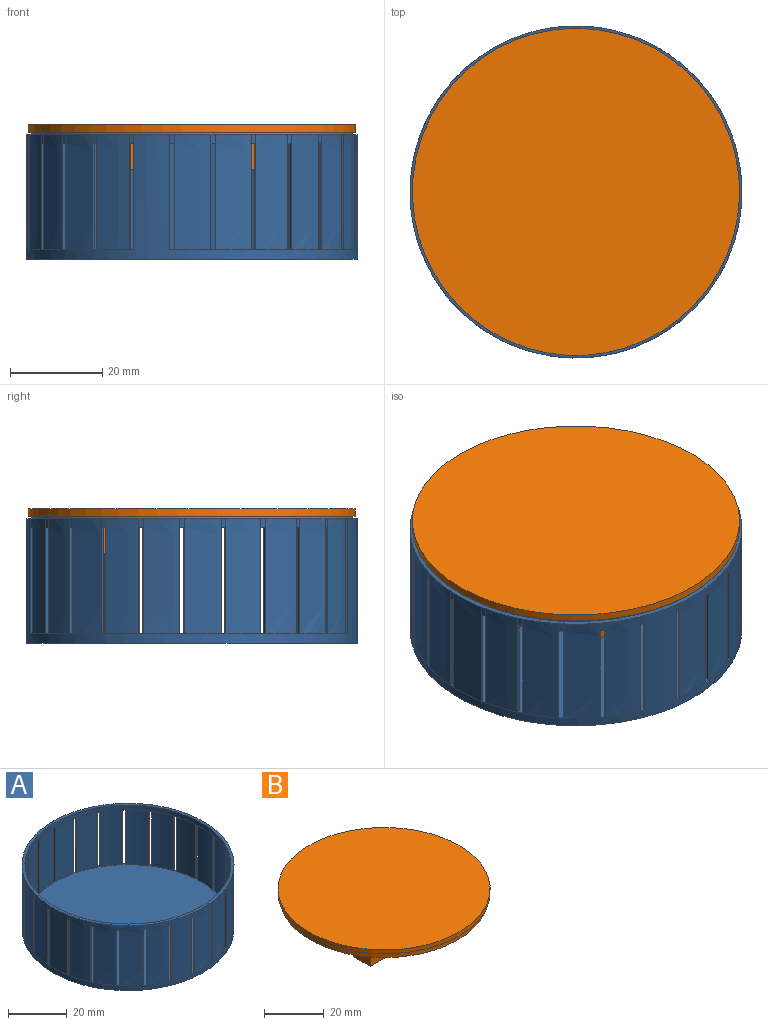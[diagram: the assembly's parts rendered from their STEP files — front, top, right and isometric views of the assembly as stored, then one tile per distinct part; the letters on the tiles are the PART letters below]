
ASSEMBLY  parts=2 mates=1
PART A: 130 faces, bbox 72x72x27 mm
  f0: cylinder r=4mm len=23mm, axis (0,0,-1), area 16.1mm2, adj f74,f75,f102,f129
  f1: cylinder r=4mm len=23mm, axis (0,0,-1), area 16.1mm2, adj f74,f75,f102,f129
  f2: cylinder r=4mm len=23mm, axis (0,0,-1), area 16.1mm2, adj f73,f75,f101,f129
  f3: cylinder r=4mm len=23mm, axis (0,0,-1), area 16.1mm2, adj f73,f75,f101,f129
  f4: cylinder r=4mm len=23mm, axis (0,0,-1), area 16.1mm2, adj f72,f75,f100,f129
  f5: cylinder r=4mm len=23mm, axis (0,0,-1), area 16.1mm2, adj f72,f75,f100,f129
  f6: cylinder r=4mm len=23mm, axis (0,0,-1), area 16.1mm2, adj f71,f75,f99,f129
  f7: cylinder r=4mm len=23mm, axis (0,0,-1), area 16.1mm2, adj f71,f75,f99,f129
  f8: cylinder r=4mm len=23mm, axis (0,0,-1), area 16.1mm2, adj f70,f75,f98,f129
  f9: cylinder r=4mm len=23mm, axis (0,0,-1), area 16.1mm2, adj f70,f75,f98,f129
  f10: cylinder r=4mm len=23mm, axis (0,0,-1), area 16.1mm2, adj f69,f75,f97,f129
  f11: cylinder r=4mm len=23mm, axis (0,0,-1), area 16.1mm2, adj f69,f75,f97,f129
  f12: cylinder r=4mm len=23mm, axis (0,0,-1), area 16.1mm2, adj f68,f75,f96,f129
  f13: cylinder r=4mm len=23mm, axis (0,0,-1), area 16.1mm2, adj f68,f75,f96,f129
  f14: cylinder r=4mm len=23mm, axis (0,0,-1), area 16.1mm2, adj f67,f75,f95,f129
  f15: cylinder r=4mm len=23mm, axis (0,0,-1), area 16.1mm2, adj f67,f75,f95,f129
  f16: cylinder r=4mm len=23mm, axis (0,0,-1), area 16.1mm2, adj f66,f75,f94,f129
  f17: cylinder r=4mm len=23mm, axis (0,0,-1), area 16.1mm2, adj f66,f75,f94,f129
  f18: cylinder r=4mm len=23mm, axis (0,0,-1), area 16.1mm2, adj f64,f75,f93,f129
  f19: cylinder r=4mm len=23mm, axis (0,0,-1), area 16.1mm2, adj f64,f75,f93,f129
  f20: cylinder r=4mm len=23mm, axis (0,0,-1), area 16.1mm2, adj f63,f75,f92,f129
  f21: cylinder r=4mm len=23mm, axis (0,0,-1), area 16.1mm2, adj f63,f75,f92,f129
  f22: cylinder r=4mm len=23mm, axis (0,0,-1), area 16.1mm2, adj f62,f75,f91,f129
  f23: cylinder r=4mm len=23mm, axis (0,0,-1), area 16.1mm2, adj f62,f75,f91,f129
  f24: cylinder r=4mm len=23mm, axis (0,0,-1), area 16.1mm2, adj f61,f75,f90,f129
  f25: cylinder r=4mm len=23mm, axis (0,0,-1), area 16.1mm2, adj f61,f75,f90,f129
  f26: cylinder r=4mm len=23mm, axis (0,0,-1), area 16.1mm2, adj f60,f75,f89,f129
  f27: cylinder r=4mm len=23mm, axis (0,0,-1), area 16.1mm2, adj f60,f75,f89,f129
  f28: cylinder r=4mm len=23mm, axis (0,0,-1), area 16.1mm2, adj f59,f75,f88,f129
  f29: cylinder r=4mm len=23mm, axis (0,0,-1), area 16.1mm2, adj f59,f75,f88,f129
  f30: cylinder r=4mm len=23mm, axis (0,0,-1), area 16.1mm2, adj f58,f75,f87,f129
  f31: cylinder r=4mm len=23mm, axis (0,0,-1), area 16.1mm2, adj f58,f75,f87,f129
  f32: cylinder r=4mm len=23mm, axis (0,0,-1), area 16.1mm2, adj f57,f75,f86,f129
  f33: cylinder r=4mm len=23mm, axis (0,0,-1), area 16.1mm2, adj f57,f75,f86,f129
  f34: cylinder r=4mm len=23mm, axis (0,0,-1), area 16.1mm2, adj f56,f75,f85,f129
  f35: cylinder r=4mm len=23mm, axis (0,0,-1), area 16.1mm2, adj f56,f75,f85,f129
  f36: cylinder r=4mm len=23mm, axis (0,0,-1), area 16.1mm2, adj f55,f75,f84,f129
  f37: cylinder r=4mm len=23mm, axis (0,0,-1), area 16.1mm2, adj f55,f75,f84,f129
  f38: cylinder r=4mm len=23mm, axis (0,0,-1), area 16.1mm2, adj f54,f75,f83,f129
  f39: cylinder r=4mm len=23mm, axis (0,0,-1), area 16.1mm2, adj f54,f75,f83,f129
  f40: cylinder r=4mm len=23mm, axis (0,0,-1), area 16.1mm2, adj f53,f75,f82,f129
  f41: cylinder r=4mm len=23mm, axis (0,0,-1), area 16.1mm2, adj f53,f75,f82,f129
  f42: cylinder r=4mm len=23mm, axis (0,0,-1), area 16.1mm2, adj f52,f75,f81,f129
  f43: cylinder r=4mm len=23mm, axis (0,0,-1), area 16.1mm2, adj f52,f75,f81,f129
  f44: cylinder r=4mm len=23mm, axis (0,0,-1), area 16.1mm2, adj f51,f75,f80,f129
  f45: cylinder r=4mm len=23mm, axis (0,0,-1), area 16.1mm2, adj f51,f75,f80,f129
  f46: cylinder r=4mm len=23mm, axis (0,0,-1), area 16.1mm2, adj f50,f75,f79,f129
  f47: cylinder r=4mm len=23mm, axis (0,0,-1), area 16.1mm2, adj f50,f75,f79,f129
  f48: cylinder r=4mm len=23mm, axis (0,0,-1), area 16.1mm2, adj f65,f75,f76,f129
  f49: cylinder r=4mm len=23mm, axis (0,0,-1), area 16.1mm2, adj f65,f75,f76,f129
  f50: cylinder r=35.3mm len=23mm, axis (0,0,-1), area 179.5mm2, adj f46,f47,f75,f129
  f51: cylinder r=35.3mm len=23mm, axis (0,0,-1), area 179.5mm2, adj f44,f45,f75,f129
  f52: cylinder r=35.3mm len=23mm, axis (0,0,-1), area 179.5mm2, adj f42,f43,f75,f129
  f53: cylinder r=35.3mm len=23mm, axis (0,0,-1), area 179.5mm2, adj f40,f41,f75,f129
  f54: cylinder r=35.3mm len=23mm, axis (0,0,-1), area 179.5mm2, adj f38,f39,f75,f129
  f55: cylinder r=35.3mm len=23mm, axis (0,0,-1), area 179.5mm2, adj f36,f37,f75,f129
  f56: cylinder r=35.3mm len=23mm, axis (0,0,-1), area 179.5mm2, adj f34,f35,f75,f129
  f57: cylinder r=35.3mm len=23mm, axis (0,0,-1), area 179.5mm2, adj f32,f33,f75,f129
  f58: cylinder r=35.3mm len=23mm, axis (0,0,-1), area 179.5mm2, adj f30,f31,f75,f129
  f59: cylinder r=35.3mm len=23mm, axis (0,0,-1), area 179.5mm2, adj f28,f29,f75,f129
  f60: cylinder r=35.3mm len=23mm, axis (0,0,-1), area 179.5mm2, adj f26,f27,f75,f129
  f61: cylinder r=35.3mm len=23mm, axis (0,0,-1), area 179.5mm2, adj f24,f25,f75,f129
  f62: cylinder r=35.3mm len=23mm, axis (0,0,-1), area 179.5mm2, adj f22,f23,f75,f129
  f63: cylinder r=35.3mm len=23mm, axis (0,0,-1), area 179.5mm2, adj f20,f21,f75,f129
  f64: cylinder r=35.3mm len=23mm, axis (0,0,-1), area 179.5mm2, adj f18,f19,f75,f129
  f65: cylinder r=35.3mm len=23mm, axis (0,0,-1), area 179.5mm2, adj f48,f49,f75,f129
  f66: cylinder r=35.3mm len=23mm, axis (0,0,-1), area 179.5mm2, adj f16,f17,f75,f129
  f67: cylinder r=35.3mm len=23mm, axis (0,0,-1), area 179.5mm2, adj f14,f15,f75,f129
  f68: cylinder r=35.3mm len=23mm, axis (0,0,-1), area 179.5mm2, adj f12,f13,f75,f129
  f69: cylinder r=35.3mm len=23mm, axis (0,0,-1), area 179.5mm2, adj f10,f11,f75,f129
  f70: cylinder r=35.3mm len=23mm, axis (0,0,-1), area 179.5mm2, adj f8,f9,f75,f129
  f71: cylinder r=35.3mm len=23mm, axis (0,0,-1), area 179.5mm2, adj f6,f7,f75,f129
  f72: cylinder r=35.3mm len=23mm, axis (0,0,-1), area 179.5mm2, adj f4,f5,f75,f129
  f73: cylinder r=35.3mm len=23mm, axis (0,0,-1), area 179.5mm2, adj f2,f3,f75,f129
  f74: cylinder r=35.3mm len=23mm, axis (0,0,-1), area 179.5mm2, adj f0,f1,f75,f129
  f75: plane 71.92x71.79mm, normal (0,0,1), area 3932.8mm2, adj f0,f1,f2,f3,f4,f5,f6,f7
  f76: cylinder r=36mm len=72mm, axis (0,0,-1), area 652.5mm2, adj f48,f49,f75,f77,f78,f79,f80,f81
  f77: plane 72x72mm, normal (0,0,-1), area 4071.5mm2, adj f76
  f78: plane 72.04x72.01mm, normal (0,0,1), area 223mm2, adj f76,f79,f80,f81,f82,f83,f84,f85
  f79: extruded ~25x7.42mm, area 200.1mm2, adj f46,f47,f76,f78,f104,f105
  f80: extruded ~25x7.92mm, area 200.1mm2, adj f44,f45,f76,f78,f105,f106
  f81: extruded ~25x7.93mm, area 200.1mm2, adj f42,f43,f76,f78,f106,f107
  f82: extruded ~25x7.44mm, area 200.1mm2, adj f40,f41,f76,f78,f107,f108
  f83: extruded ~25x6.48mm, area 200.1mm2, adj f38,f39,f76,f78,f108,f109
  f84: extruded ~25x6.14mm, area 200.1mm2, adj f36,f37,f76,f78,f109,f110
  f85: extruded ~25x7.22mm, area 200.1mm2, adj f34,f35,f76,f78,f110,f111
  f86: extruded ~25x7.84mm, area 200.1mm2, adj f32,f33,f76,f78,f111,f112
  f87: extruded ~25x7.97mm, area 200.1mm2, adj f30,f31,f76,f78,f112,f113
  f88: extruded ~25x7.6mm, area 200.1mm2, adj f28,f29,f76,f78,f113,f114
  f89: extruded ~25x6.76mm, area 200.1mm2, adj f26,f27,f76,f78,f114,f115
  f90: extruded ~25x5.81mm, area 200.1mm2, adj f24,f25,f76,f78,f115,f116
  f91: extruded ~25x6.99mm, area 200.1mm2, adj f22,f23,f76,f78,f116,f117
  f92: extruded ~25x7.73mm, area 200.1mm2, adj f20,f21,f76,f78,f117,f118
  f93: extruded ~25x7.99mm, area 200.1mm2, adj f18,f19,f76,f78,f118,f119
  f94: extruded ~25x7.01mm, area 200.1mm2, adj f16,f17,f76,f78,f103,f120
  f95: extruded ~25x5.84mm, area 200.1mm2, adj f14,f15,f76,f78,f120,f121
  f96: extruded ~25x6.73mm, area 200.1mm2, adj f12,f13,f76,f78,f121,f122
  f97: extruded ~25x7.59mm, area 200.1mm2, adj f10,f11,f76,f78,f122,f123
  f98: extruded ~25x7.97mm, area 200.1mm2, adj f8,f9,f76,f78,f123,f124
  f99: extruded ~25x7.85mm, area 200.1mm2, adj f6,f7,f76,f78,f124,f125
  f100: extruded ~25x7.24mm, area 200.1mm2, adj f4,f5,f76,f78,f125,f126
  f101: extruded ~25x6.17mm, area 200.1mm2, adj f2,f3,f76,f78,f126,f127
  f102: extruded ~25x6.45mm, area 200.1mm2, adj f0,f1,f76,f78,f104,f127
  f103: extruded ~2x0.97mm, area 2.1mm2, adj f76,f78,f94,f129
  f104: extruded ~2x0.91mm, area 2.1mm2, adj f78,f79,f102,f129
  f105: extruded ~2x1.01mm, area 2.1mm2, adj f78,f79,f80,f129
  f106: extruded ~2x1.04mm, area 2.1mm2, adj f78,f80,f81,f129
  f107: extruded ~2x1.01mm, area 2.1mm2, adj f78,f81,f82,f129
  f108: extruded ~2x0.92mm, area 2.1mm2, adj f78,f82,f83,f129
  f109: extruded ~2x0.76mm, area 2.1mm2, adj f78,f83,f84,f129
  f110: extruded ~2x0.88mm, area 2.1mm2, adj f78,f84,f85,f129
  f111: extruded ~2x0.99mm, area 2.1mm2, adj f78,f85,f86,f129
  f112: extruded ~2x1.04mm, area 2.1mm2, adj f78,f86,f87,f129
  f113: extruded ~2x1.03mm, area 2.1mm2, adj f78,f87,f88,f129
  f114: extruded ~2x0.95mm, area 2.1mm2, adj f78,f88,f89,f129
  f115: extruded ~2x0.81mm, area 2.1mm2, adj f78,f89,f90,f129
  f116: extruded ~2x0.84mm, area 2.1mm2, adj f78,f90,f91,f129
  f117: extruded ~2x0.97mm, area 2.1mm2, adj f78,f91,f92,f129
  f118: extruded ~2x1.04mm, area 2.1mm2, adj f78,f92,f93,f129
  f119: extruded ~2x1.04mm, area 2.1mm2, adj f76,f78,f93,f129
  f120: extruded ~2x0.85mm, area 2.1mm2, adj f78,f94,f95,f129
  f121: extruded ~2x0.8mm, area 2.1mm2, adj f78,f95,f96,f129
  f122: extruded ~2x0.94mm, area 2.1mm2, adj f78,f96,f97,f129
  f123: extruded ~2x1.02mm, area 2.1mm2, adj f78,f97,f98,f129
  f124: extruded ~2x1.04mm, area 2.1mm2, adj f78,f98,f99,f129
  f125: extruded ~2x0.99mm, area 2.1mm2, adj f78,f99,f100,f129
  f126: extruded ~2x0.88mm, area 2.1mm2, adj f78,f100,f101,f129
  f127: extruded ~2x0.76mm, area 2.1mm2, adj f78,f101,f102,f129
  f128: cylinder r=35mm len=70mm, axis (0,0,1), area 439.8mm2, adj f78,f129
  f129: plane 71.92x71.79mm, normal (0,0,-1), area 84.4mm2, adj f0,f1,f2,f3,f4,f5,f6,f7
PART B: 33 faces, bbox 71x71x9.6 mm
  f0: plane 69.7x69.7mm, normal (0,0,-1), area 3728.5mm2, adj f1,f5,f6,f7,f8,f9,f10,f12
  f1: cylinder r=34.85mm len=69.7mm, axis (0,0,-1), area 437.9mm2, adj f0,f4
  f2: cylinder r=35.5mm len=71mm, axis (0,0,-1), area 356.9mm2, adj f3,f4
  f3: plane 71x71mm, normal (0,0,1), area 3959.2mm2, adj f2
  f4: plane 71x71mm, normal (0,0,-1), area 143.7mm2, adj f1,f2
  f5: plane 8x6mm, normal (0,-1,0), area 48mm2, adj f0,f6,f10,f11
  f6: plane 6x1.5mm, normal (-1,0,0), area 9mm2, adj f0,f5,f7,f11
  f7: plane 6.5x6mm, normal (0,1,0), area 39mm2, adj f0,f6,f8,f11
  f8: plane 6.5x6mm, normal (-1,0,0), area 39mm2, adj f0,f7,f9,f11
  f9: plane 6x1.5mm, normal (0,1,0), area 9mm2, adj f0,f8,f10,f11
  f10: plane 8x6mm, normal (1,0,0), area 48mm2, adj f0,f5,f9,f11
  f11: plane 8x8mm, normal (0,0,-1), area 21.7mm2, adj f5,f6,f7,f8,f9,f10
  f12: plane 6.5x6mm, normal (0,-1,0), area 39mm2, adj f0,f13,f17,f18
  f13: plane 6x1.5mm, normal (-1,0,0), area 9mm2, adj f0,f12,f14,f18
  f14: plane 8x6mm, normal (0,1,0), area 48mm2, adj f0,f13,f15,f18
  f15: plane 8x6mm, normal (1,0,0), area 48mm2, adj f0,f14,f16,f18
  f16: plane 6x1.5mm, normal (0,-1,0), area 9mm2, adj f0,f15,f17,f18
  f17: plane 6.5x6mm, normal (-1,0,0), area 39mm2, adj f0,f12,f16,f18
  f18: plane 8x8mm, normal (0,0,-1), area 21.7mm2, adj f12,f13,f14,f15,f16,f17
  f19: plane 6x1.5mm, normal (1,0,0), area 9mm2, adj f0,f20,f24,f25
  f20: plane 8x6mm, normal (0,-1,0), area 48mm2, adj f0,f19,f21,f25
  f21: plane 8x6mm, normal (-1,0,0), area 48mm2, adj f0,f20,f22,f25
  f22: plane 6x1.5mm, normal (0,1,0), area 9mm2, adj f0,f21,f23,f25
  f23: plane 6.5x6mm, normal (1,0,0), area 39mm2, adj f0,f22,f24,f25
  f24: plane 6.5x6mm, normal (0,1,0), area 39mm2, adj f0,f19,f23,f25
  f25: plane 8x8mm, normal (0,0,-1), area 21.7mm2, adj f19,f20,f21,f22,f23,f24
  f26: plane 6x1.5mm, normal (0,-1,0), area 9mm2, adj f0,f27,f31,f32
  f27: plane 8x6mm, normal (-1,0,0), area 48mm2, adj f0,f26,f28,f32
  f28: plane 8x6mm, normal (0,1,0), area 48mm2, adj f0,f27,f29,f32
  f29: plane 6x1.5mm, normal (1,0,0), area 9mm2, adj f0,f28,f30,f32
  f30: plane 6.5x6mm, normal (0,-1,0), area 39mm2, adj f0,f29,f31,f32
  f31: plane 6.5x6mm, normal (1,0,0), area 39mm2, adj f0,f26,f30,f32
  f32: plane 8x8mm, normal (0,0,-1), area 21.7mm2, adj f26,f27,f28,f29,f30,f31
PLACE A t=(-37.68,42.99,0)mm fixed
PLACE B rot(axis=(0,0,1),90deg) t=(-37.68,42.99,25.5)mm
MATE cylindrical B.f1 <-> A.f76  axis (0,0,-1) through (-37.68,42.99,25.5)mm
